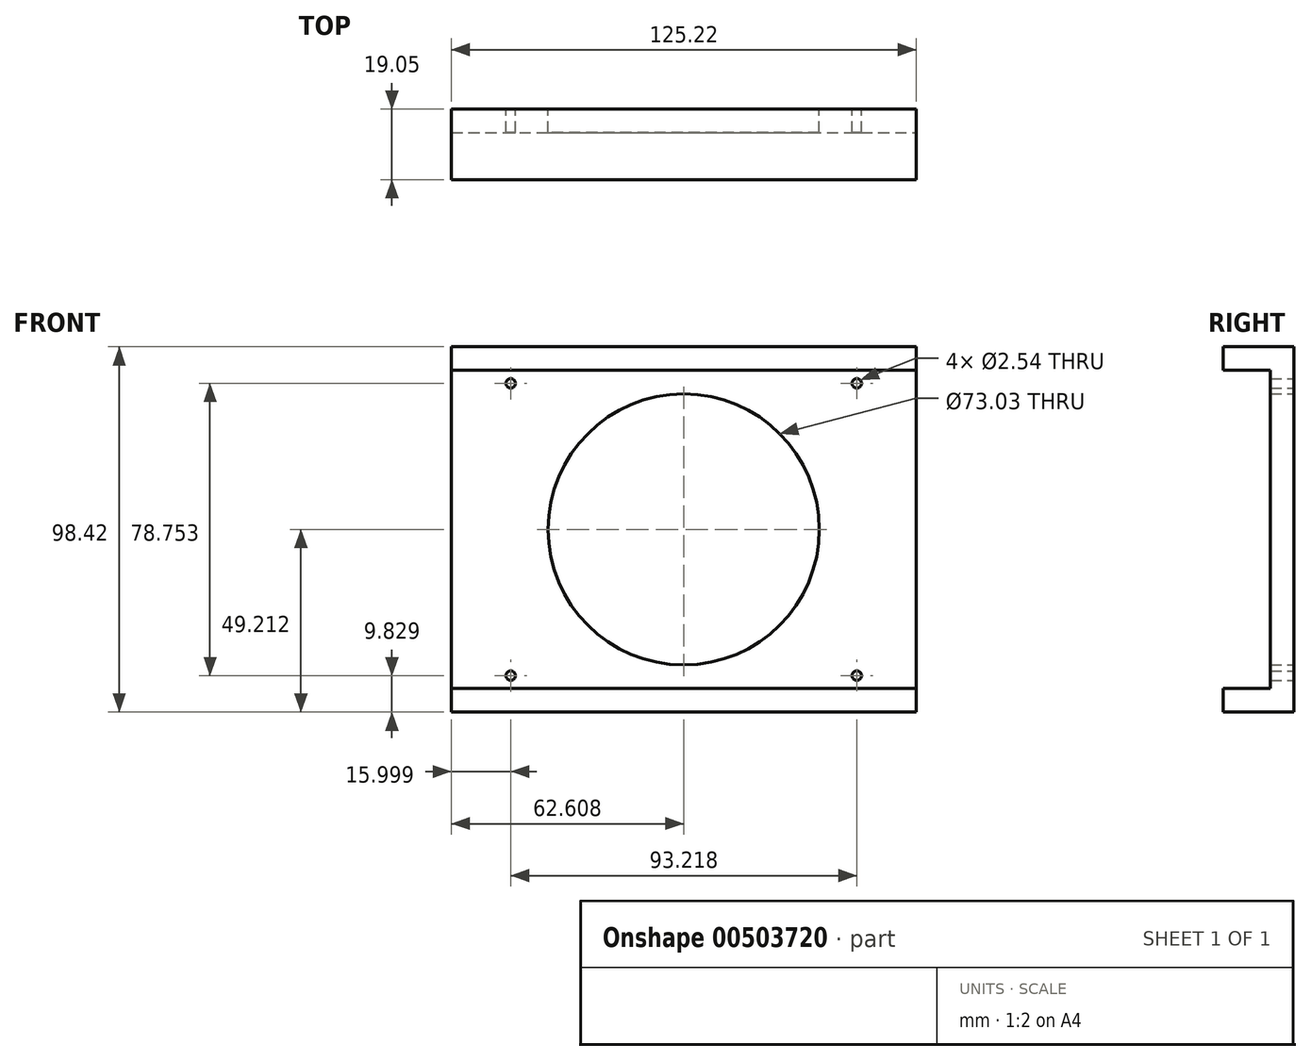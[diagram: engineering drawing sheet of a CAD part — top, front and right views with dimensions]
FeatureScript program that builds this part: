
annotation { "Feature Type Name" : "Feature", "Feature Type Description" : "" }
export const myFeature = defineFeature(function(context is Context, id is Id, definition is map)
    precondition{}
    {
        {
            var Q0;
            Q0=qCreatedBy(makeId("Front.planeOp"),FACE);
            var sketch = newSketch(context, id + "F0", { "sketchPlane" : qUnion([Q0])});
            skCircle(sketch, "E0", {"center": v(-372.76, 95.49) * mm, "radius": 1.27 * mm});
            skCircle(sketch, "E1", {"center": v(-279.54, 16.76) * mm, "radius": 1.27 * mm});
            skCircle(sketch, "E2", {"center": v(-372.76, 16.75) * mm, "radius": 1.27 * mm});
            skCircle(sketch, "E3", {"center": v(-279.54, 95.5) * mm, "radius": 1.27 * mm});
            skLineSegment(sketch, "E4.bottom", {"start": v(-376.06, 99.12) * mm, "end": v(-276.24, 99.12) * mm});
            skLineSegment(sketch, "E4.top", {"start": v(-376.06, 13.14) * mm, "end": v(-276.24, 13.14) * mm});
            skLineSegment(sketch, "E4.left", {"start": v(-376.06, 99.12) * mm, "end": v(-376.06, 13.14) * mm});
            skLineSegment(sketch, "E4.right", {"start": v(-276.24, 99.12) * mm, "end": v(-276.24, 13.14) * mm});
            skLineSegment(sketch, "E5.bottom", {"start": v(-388.76, 105.34) * mm, "end": v(-263.54, 105.34) * mm});
            skLineSegment(sketch, "E5.top", {"start": v(-388.76, 6.92) * mm, "end": v(-263.54, 6.92) * mm});
            skLineSegment(sketch, "E5.left", {"start": v(-388.76, 105.34) * mm, "end": v(-388.76, 6.92) * mm});
            skLineSegment(sketch, "E5.right", {"start": v(-263.54, 105.34) * mm, "end": v(-263.54, 6.92) * mm});
            skCircle(sketch, "E6", {"center": v(-326.15, 56.13) * mm, "radius": 36.51 * mm});
            skSolve(sketch);
        }
        {
            var Q0;
            Q0=makeQuery(id+"F0.imprint","IMPRINT",FACE,{"disambiguationData":[TD([[makeQuery(id+"F0.imprint","IMPRINT",EDGE,{"derivedFrom":sQuery(id+"F0.wireOp",EDGE,"E4.bottom")}),1.0]])]});
            var Q1;
            Q1=makeQuery(id+"F0.imprint","IMPRINT",FACE,{"disambiguationData":[TD([[makeQuery(id+"F0.imprint","IMPRINT",EDGE,{"derivedFrom":sQuery(id+"F0.wireOp",EDGE,"E0")}),-1.0]])]});
            extrude(context, id + "F1", {"entities" : qUnion([Q0, Q1]), "depth" : 19.05 * mm});
        }
        {
            var Q0;
            Q0=makeQuery(id+"F1.opExtrude","CAP_FACE",FACE,{"disambiguationData":[OSD([sQuery(id+"F0.wireOp",EDGE,"E0"),sQuery(id+"F0.wireOp",EDGE,"E1"),sQuery(id+"F0.wireOp",EDGE,"E2"),sQuery(id+"F0.wireOp",EDGE,"E3"),sQuery(id+"F0.wireOp",EDGE,"E5.bottom"),sQuery(id+"F0.wireOp",EDGE,"E5.top"),sQuery(id+"F0.wireOp",EDGE,"E5.left"),sQuery(id+"F0.wireOp",EDGE,"E5.right")])],"isStart":false});
            var sketch = newSketch(context, id + "F2", { "sketchPlane" : qUnion([Q0])});
            skLineSegment(sketch, "E7.bottom", {"start": v(-429.58, 99) * mm, "end": v(130.28, 99) * mm});
            skLineSegment(sketch, "E7.top", {"start": v(-429.58, 13.27) * mm, "end": v(130.28, 13.27) * mm});
            skLineSegment(sketch, "E7.left", {"start": v(-429.58, 99) * mm, "end": v(-429.58, 13.27) * mm});
            skLineSegment(sketch, "E7.right", {"start": v(130.28, 99) * mm, "end": v(130.28, 13.27) * mm});
            skSolve(sketch);
        }
        {
            var Q0;
            Q0 = qSketchRegion(id + "F2", true);
            extrude(context, id + "F3", {"entities" : qUnion([Q0]), "operationType" : NewBodyOperationType.REMOVE, "oppositeDirection" : true, "depth" : 12.7 * mm});
        }
        {
            var Q0;
            Q0=makeQuery(id+"F2.imprint","IMPRINT",FACE,{"disambiguationData":[TD([[makeQuery(id+"F2.imprint","IMPRINT",EDGE,{"derivedFrom":makeQuery(id+"F1.opExtrude","CAP_EDGE",EDGE,{"disambiguationData":[OSD([sQuery(id+"F0.wireOp",EDGE,"E0")])],"isStart":false})}),-1.0]])]});
            extrude(context, id + "F4", {"entities" : qUnion([Q0]), "operationType" : NewBodyOperationType.REMOVE, "oppositeDirection" : true, "depth" : 12.7 * mm});
        }
    });
